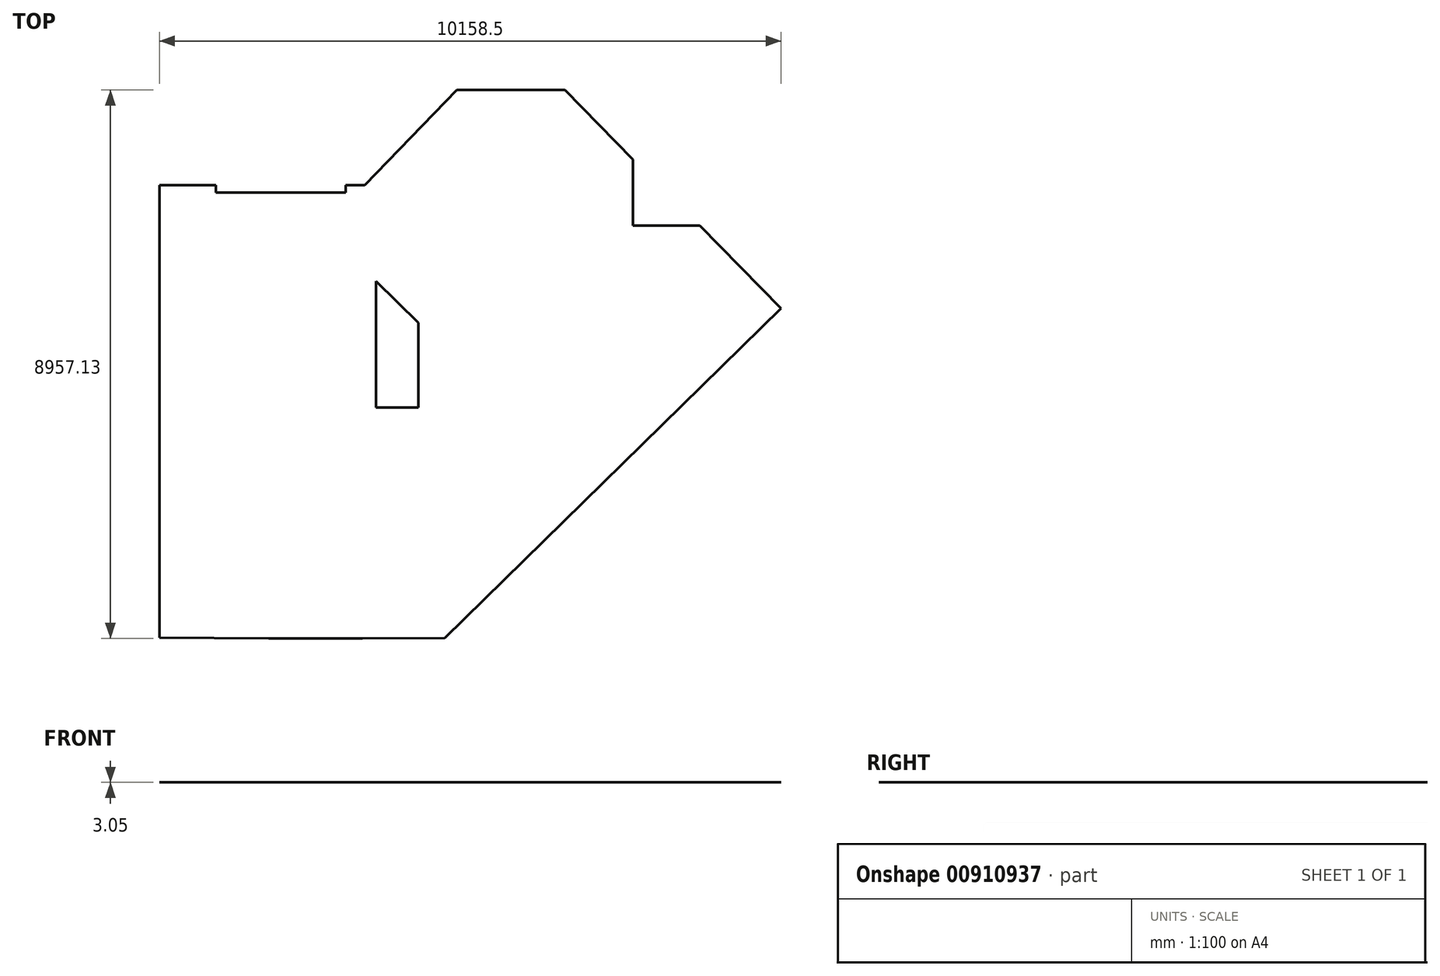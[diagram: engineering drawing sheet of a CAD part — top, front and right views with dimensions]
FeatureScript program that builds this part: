
annotation { "Feature Type Name" : "Feature", "Feature Type Description" : "" }
export const myFeature = defineFeature(function(context is Context, id is Id, definition is map)
    precondition{}
    {
        {
            var Q0;
            Q0=qCreatedBy(makeId("Top.planeOp"),FACE);
            var sketch = newSketch(context, id + "F0", { "sketchPlane" : qUnion([Q0])});
            skLineSegment(sketch, "E0", {"start": v(-1784, 2249.23) * mm, "end": v(-1784, -2341.36) * mm});
            skLineSegment(sketch, "E1", {"start": v(-1784, 2249.23) * mm, "end": v(1568.8, 2249.23) * mm});
            skLineSegment(sketch, "E2", {"start": v(1568.8, 2249.23) * mm, "end": v(1568.8, 865.9) * mm});
            skLineSegment(sketch, "E3", {"start": v(1568.8, 865.9) * mm, "end": v(2449.06, 0) * mm});
            skLineSegment(sketch, "E4", {"start": v(2449.06, 0) * mm, "end": v(2449.06, -1382.13) * mm});
            skLineSegment(sketch, "E5", {"start": v(2449.06, -1382.13) * mm, "end": v(1756.28, -1382.13) * mm});
            skLineSegment(sketch, "E6", {"start": v(1756.28, -1382.13) * mm, "end": v(1756.28, -2328.04) * mm});
            skLineSegment(sketch, "E7", {"start": v(1756.28, -2328.04) * mm, "end": v(2409.09, -2328.04) * mm});
            skLineSegment(sketch, "E8", {"start": v(690.47, -2341.36) * mm, "end": v(0, -2341.36) * mm});
            skLineSegment(sketch, "E9", {"start": v(0, -2341.36) * mm, "end": v(0, -3102.67) * mm});
            skLineSegment(sketch, "E10", {"start": v(0, -3948.3) * mm, "end": v(0, -5154.38) * mm});
            skLineSegment(sketch, "E11", {"start": v(0, -5154.38) * mm, "end": v(1534.42, -5154.38) * mm});
            skLineSegment(sketch, "E12", {"start": v(1534.42, -5154.38) * mm, "end": v(1534.42, -3955.24) * mm});
            skLineSegment(sketch, "E13", {"start": v(4179.8, -3831.73) * mm, "end": v(3718.2, -3386.6) * mm});
            skLineSegment(sketch, "E14", {"start": v(3718.2, -3386.6) * mm, "end": v(3404.97, -3386.6) * mm});
            skLineSegment(sketch, "E15", {"start": v(3404.97, -3386.6) * mm, "end": v(3404.97, -3609.17) * mm});
            skLineSegment(sketch, "E16", {"start": v(3421.46, -4680.75) * mm, "end": v(3421.46, -4458.19) * mm});
            skLineSegment(sketch, "E17", {"start": v(3365.98, -2083.97) * mm, "end": v(3365.98, -1348.78) * mm});
            skLineSegment(sketch, "E18", {"start": v(3365.98, -1348.78) * mm, "end": v(4684.6, -57.17) * mm});
            skLineSegment(sketch, "E19", {"start": v(4684.6, -57.17) * mm, "end": v(5020.76, -400.35) * mm});
            skLineSegment(sketch, "E20", {"start": v(5927.84, -1303.97) * mm, "end": v(6357.1, -1742.2) * mm});
            skLineSegment(sketch, "E21", {"start": v(6357.1, -1742.2) * mm, "end": v(8374.48, 233.85) * mm});
            skLineSegment(sketch, "E22", {"start": v(8374.48, 233.85) * mm, "end": v(7047.72, 1588.36) * mm});
            skLineSegment(sketch, "E23", {"start": v(7047.72, 1588.36) * mm, "end": v(5956.01, 1588.36) * mm});
            skLineSegment(sketch, "E24", {"start": v(5956.01, 1588.36) * mm, "end": v(5956.01, 2667.54) * mm});
            skLineSegment(sketch, "E25", {"start": v(5956.01, 2667.54) * mm, "end": v(4844.06, 3802.75) * mm});
            skLineSegment(sketch, "E26", {"start": v(4844.06, 3802.75) * mm, "end": v(3078.53, 3802.75) * mm});
            skLineSegment(sketch, "E27", {"start": v(3078.53, 3802.75) * mm, "end": v(1568.8, 2249.23) * mm});
            skLineSegment(sketch, "E28", {"start": v(0, -2341.36) * mm, "end": v(-1784, -2341.36) * mm});
            skLineSegment(sketch, "E29", {"start": v(-1784, -2341.36) * mm, "end": v(-1784, -5145.35) * mm});
            skLineSegment(sketch, "E30", {"start": v(-1784, -5145.35) * mm, "end": v(0, -5154.38) * mm});
            skLineSegment(sketch, "E31", {"start": v(619.31, -2341.36) * mm, "end": v(619.31, -1707.35) * mm});
            skLineSegment(sketch, "E32", {"start": v(619.31, -1707.35) * mm, "end": v(-1784, -1707.35) * mm});
            skLineSegment(sketch, "E33", {"start": v(6357.1, -1742.2) * mm, "end": v(2877.59, -5150.42) * mm});
            skLineSegment(sketch, "E34", {"start": v(2877.59, -5150.42) * mm, "end": v(1534.42, -5154.38) * mm});
            skLineSegment(sketch, "E35", {"start": v(1756.28, -1382.13) * mm, "end": v(1756.28, 681.49) * mm});
            skLineSegment(sketch, "E36", {"start": v(-859.34, 2445.46) * mm, "end": v(-859.34, 2127.93) * mm});
            skLineSegment(sketch, "E37", {"start": v(-859.34, 2127.93) * mm, "end": v(1257.54, 2127.93) * mm});
            skLineSegment(sketch, "E38", {"start": v(1257.54, 2127.93) * mm, "end": v(1257.54, 2493.97) * mm});
            skSolve(sketch);
        }
        {
            var Q0;
            Q0=sQuery(id+"F0.wireOp",EDGE,"E27");
            var Q1;
            Q1=sQuery(id+"F0.wireOp",EDGE,"E1");
            var Q2;
            Q2=sQuery(id+"F0.wireOp",EDGE,"E26");
            var Q3;
            Q3=sQuery(id+"F0.wireOp",EDGE,"E25");
            var Q4;
            Q4=sQuery(id+"F0.wireOp",EDGE,"E24");
            var Q5;
            Q5=sQuery(id+"F0.wireOp",EDGE,"E23");
            var Q6;
            Q6=sQuery(id+"F0.wireOp",EDGE,"E22");
            var Q7;
            Q7=sQuery(id+"F0.wireOp",EDGE,"E21");
            var Q8;
            Q8=sQuery(id+"F0.wireOp",EDGE,"E20");
            var Q9;
            Q9=sQuery(id+"F0.wireOp",EDGE,"E19");
            var Q10;
            Q10=sQuery(id+"F0.wireOp",EDGE,"E18");
            var Q11;
            Q11=sQuery(id+"F0.wireOp",EDGE,"E17");
            var Q12;
            Q12=sQuery(id+"F0.wireOp",EDGE,"E12");
            var Q13;
            Q13=sQuery(id+"F0.wireOp",EDGE,"E11");
            var Q14;
            Q14=sQuery(id+"F0.wireOp",EDGE,"E30");
            var Q15;
            Q15=sQuery(id+"F0.wireOp",EDGE,"E29");
            var Q16;
            Q16=sQuery(id+"F0.wireOp",EDGE,"E28");
            var Q17;
            Q17=sQuery(id+"F0.wireOp",EDGE,"E8");
            var Q18;
            Q18=sQuery(id+"F0.wireOp",EDGE,"E16");
            var Q19;
            Q19=sQuery(id+"F0.wireOp",EDGE,"E15");
            var Q20;
            Q20=sQuery(id+"F0.wireOp",EDGE,"E14");
            var Q21;
            Q21=sQuery(id+"F0.wireOp",EDGE,"E13");
            extrude(context, id + "F1", {"bodyType" : ToolBodyType.SURFACE, "surfaceEntities" : qUnion([Q0, Q1, Q2, Q3, Q4, Q5, Q6, Q7, Q8, Q9, Q10, Q11, Q12, Q13, Q14, Q15, Q16, Q17, Q18, Q19, Q20, Q21]), "depth" : 3048 * mm, "offsetDistance" : 30.48 * mm});
        }
        {
            var Q0;
            Q0=sQuery(id+"F0.wireOp",EDGE,"E2");
            var Q1;
            Q1=sQuery(id+"F0.wireOp",EDGE,"E3");
            var Q2;
            Q2=sQuery(id+"F0.wireOp",EDGE,"E4");
            var Q3;
            Q3=sQuery(id+"F0.wireOp",EDGE,"E5");
            var Q4;
            Q4=sQuery(id+"F0.wireOp",EDGE,"E6");
            var Q5;
            Q5=sQuery(id+"F0.wireOp",EDGE,"E7");
            var Q6;
            Q6=sQuery(id+"F0.wireOp",EDGE,"E0");
            extrude(context, id + "F2", {"bodyType" : ToolBodyType.SURFACE, "surfaceEntities" : qUnion([Q0, Q1, Q2, Q3, Q4, Q5, Q6]), "depth" : 3048 * mm, "offsetDistance" : 30.48 * mm});
        }
        {
            var Q0;
            Q0=sQuery(id+"F0.wireOp",EDGE,"E32");
            var Q1;
            Q1=sQuery(id+"F0.wireOp",EDGE,"E31");
            extrude(context, id + "F3", {"bodyType" : ToolBodyType.SURFACE, "surfaceEntities" : qUnion([Q0, Q1]), "depth" : 3048 * mm, "offsetDistance" : 30.48 * mm});
        }
        {
            var Q0;
            {var subQ1=sQuery(id+"F0.wireOp",EDGE,"E1");Q0=makeQuery(id+"F0.imprint","IMPRINT",FACE,{"disambiguationData":[TD([[makeQuery(id+"F0.imprint","IMPRINT",EDGE,{"derivedFrom":subQ1}),-1.0]])]});}
            var Q1;
            {var subQ1=sQuery(id+"F0.wireOp",EDGE,"E28");Q1=makeQuery(id+"F0.imprint","IMPRINT",FACE,{"disambiguationData":[TD([[makeQuery(id+"F0.imprint","IMPRINT",EDGE,{"derivedFrom":subQ1}),-1.0]])]});}
            var Q2;
            Q2=sQuery(id+"F0.wireOp",EDGE,"E30");
            var Q3;
            Q3=sQuery(id+"F0.wireOp",EDGE,"E11");
            var Q4;
            Q4=sQuery(id+"F0.wireOp",EDGE,"E34");
            var Q5;
            Q5=sQuery(id+"F0.wireOp",EDGE,"E33");
            var Q6;
            Q6=sQuery(id+"F0.wireOp",EDGE,"E21");
            var Q7;
            Q7=sQuery(id+"F0.wireOp",EDGE,"E22");
            var Q8;
            Q8=sQuery(id+"F0.wireOp",EDGE,"E23");
            var Q9;
            Q9=sQuery(id+"F0.wireOp",EDGE,"E24");
            var Q10;
            Q10=sQuery(id+"F0.wireOp",EDGE,"E25");
            var Q11;
            Q11=sQuery(id+"F0.wireOp",EDGE,"E26");
            var Q12;
            Q12=sQuery(id+"F0.wireOp",EDGE,"E27");
            var Q13;
            Q13=sQuery(id+"F0.wireOp",EDGE,"E1");
            var Q14;
            Q14=sQuery(id+"F0.wireOp",EDGE,"E0");
            var Q15;
            Q15=sQuery(id+"F0.wireOp",EDGE,"E29");
            extrude(context, id + "F4", {"entities" : qUnion([Q0, Q1]), "surfaceEntities" : qUnion([Q2, Q3, Q4, Q5, Q6, Q7, Q8, Q9, Q10, Q11, Q12, Q13, Q14, Q15]), "oppositeDirection" : true, "depth" : 3.05 * mm, "offsetDistance" : 30.48 * mm});
        }
        {
            var Q0;
            Q0=sQuery(id+"F0.wireOp",EDGE,"E35");
            extrude(context, id + "F5", {"bodyType" : ToolBodyType.SURFACE, "surfaceEntities" : qUnion([Q0]), "depth" : 3048 * mm, "offsetDistance" : 30.48 * mm});
        }
        {
            var Q0;
            Q0=sQuery(id+"F0.wireOp",EDGE,"E36");
            var Q1;
            Q1=sQuery(id+"F0.wireOp",EDGE,"E38");
            var Q2;
            Q2=sQuery(id+"F0.wireOp",EDGE,"E37");
            extrude(context, id + "F6", {"bodyType" : ToolBodyType.SURFACE, "surfaceEntities" : qUnion([Q0, Q1, Q2]), "depth" : 3048 * mm, "offsetDistance" : 30.48 * mm});
        }
        {
            var Q0;
            Q0=sQuery(id+"F0.wireOp",EDGE,"E9");
            var Q1;
            Q1=sQuery(id+"F0.wireOp",EDGE,"E10");
            extrude(context, id + "F7", {"bodyType" : ToolBodyType.SURFACE, "surfaceEntities" : qUnion([Q0, Q1]), "depth" : 3048 * mm, "offsetDistance" : 30.48 * mm});
        }
    });
